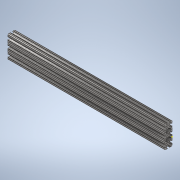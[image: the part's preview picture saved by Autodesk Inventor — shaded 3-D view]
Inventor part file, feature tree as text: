
AUTODESK INVENTOR PART (.ipt)
format: ipt  version: 2020 (Build 240168000, 168)  size: 382,464 bytes
history: native  units: in
note: dims shown in document units (in); Inventor stores cm internally (conversion verified against a paired STEP export)
features: sketch x2, extrude x1
ambient origin geometry x8: Origin, YZ Plane, XZ Plane, XY Plane, X Axis, Y Axis, Z Axis, Center Point
bodies: Solid1 (feature_tree)
feature tree (3):
  extrude  "Extrusion1"  [1 undecoded]
  sketch  "Sketch2"
  sketch  "Sketch1"  dims[d0=21.0in d1=0.0in]
note: 1 required parameter value undecoded (feature->parameter linkage not recoverable at this tier; creation-order binding heuristic only, values carry confidence <= 0.55)
